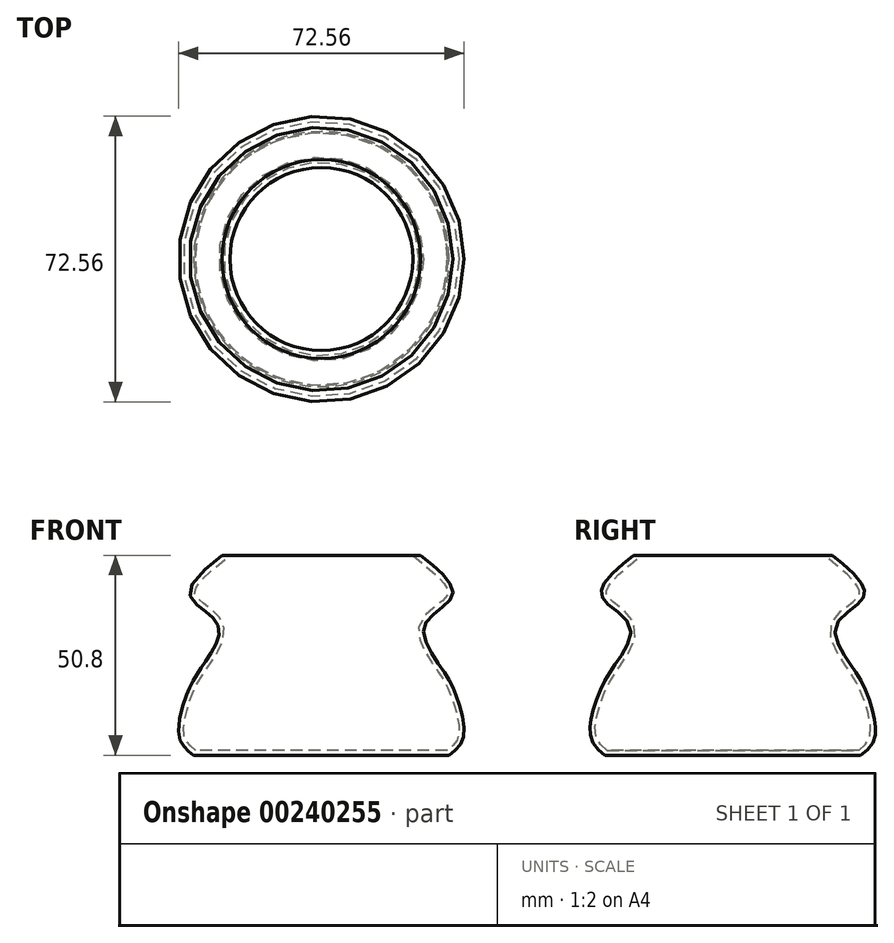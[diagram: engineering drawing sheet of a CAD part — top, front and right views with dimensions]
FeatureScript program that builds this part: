
annotation { "Feature Type Name" : "Feature", "Feature Type Description" : "" }
export const myFeature = defineFeature(function(context is Context, id is Id, definition is map)
    precondition{}
    {
        {
            var Q0;
            Q0=qCreatedBy(makeId("Front.planeOp"),FACE);
            var sketch = newSketch(context, id + "F0", { "sketchPlane" : qUnion([Q0])});
            skFitSpline(sketch, "E0", {"points": [v(-25.25, 21.96) * mm, v(-33.36, 11.7) * mm, v(-26.17, 4.05) * mm, v(-30.76, -6.96) * mm, v(-34.27, -13.7) * mm, v(-36.11, -24.25) * mm, v(-32.44, -28.84) * mm], "startDerivative": vector(-70.54, -57.28) * mm, "endDerivative": vector(36.95, -28.45) * mm});
            skLineSegment(sketch, "E1", {"start": v(-25.25, 21.96) * mm, "end": v(0, 21.96) * mm});
            skLineSegment(sketch, "E2", {"start": v(0, 21.96) * mm, "end": v(0, -28.84) * mm});
            skLineSegment(sketch, "E3", {"start": v(0, -28.84) * mm, "end": v(-32.44, -28.84) * mm});
            skSolve(sketch);
        }
        {
            var Q0;
            Q0=makeQuery(id+"F0.imprint","IMPRINT",FACE,{"disambiguationData":[TD([[makeQuery(id+"F0.imprint","IMPRINT",EDGE,{"derivedFrom":sQuery(id+"F0.wireOp",EDGE,"E0")}),1.0]])]});
            var Q1;
            Q1=sQuery(id+"F0.wireOp",EDGE,"E2");
            revolve(context, id + "F1", {"entities" : qUnion([Q0]), "axis" : qUnion([Q1]), "revolveType" : RevolveType.FULL});
        }
        {
            var Q0;
            Q0=qCreatedBy(makeId("Top.planeOp"),FACE);
            var sketch = newSketch(context, id + "F2", { "sketchPlane" : qUnion([Q0])});
            skCircle(sketch, "E4", {"center": v(0, 0) * mm, "radius": 47.53 * mm});
            skSolve(sketch);
        }
        {
            var Q0;
            Q0=makeQuery(id+"F1.opRevolve","SWEPT_FACE",FACE,{"disambiguationData":[OSD([sQuery(id+"F0.wireOp",EDGE,"E1")])]});
            shell(context, id + "F3", {"entities" : qUnion([Q0]), "thickness" : 1.27 * mm});
        }
    });
